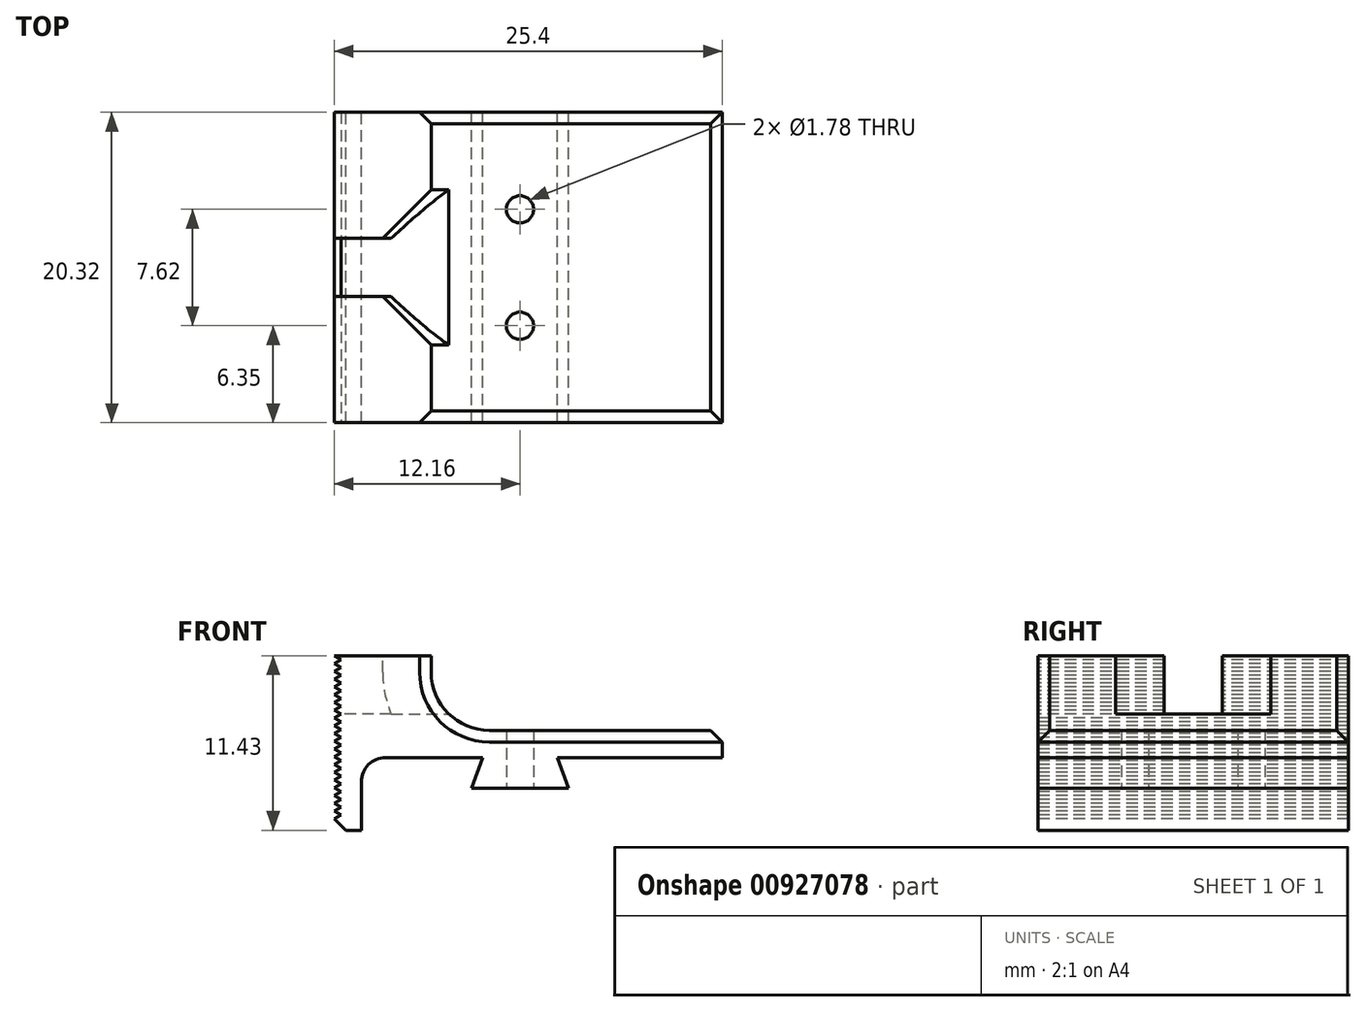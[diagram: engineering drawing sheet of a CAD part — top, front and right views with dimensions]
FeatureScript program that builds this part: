
annotation { "Feature Type Name" : "Feature", "Feature Type Description" : "" }
export const myFeature = defineFeature(function(context is Context, id is Id, definition is map)
    precondition{}
    {
        {
            var Q0;
            Q0=qCreatedBy(makeId("Front.planeOp"),FACE);
            var sketch = newSketch(context, id + "F0", { "sketchPlane" : qUnion([Q0])});
            skLineSegment(sketch, "E0", {"start": v(-0.44, 0) * mm, "end": v(-1.17, -2) * mm});
            skLineSegment(sketch, "E1", {"start": v(-1.17, -2) * mm, "end": v(5.18, -2) * mm});
            skLineSegment(sketch, "E2", {"start": v(5.18, -2) * mm, "end": v(4.44, 0) * mm});
            skLineSegment(sketch, "E3", {"start": v(4.44, 0) * mm, "end": v(15.24, 0) * mm});
            skLineSegment(sketch, "E4", {"start": v(15.24, 0) * mm, "end": v(15.24, 1.78) * mm});
            skLineSegment(sketch, "E5", {"start": v(15.24, 1.78) * mm, "end": v(-3.81, 1.78) * mm});
            skLineSegment(sketch, "E6", {"start": v(-3.81, 1.78) * mm, "end": v(-3.81, 6.67) * mm});
            skLineSegment(sketch, "E7", {"start": v(-3.81, 6.67) * mm, "end": v(-10.16, 6.67) * mm});
            skLineSegment(sketch, "E8", {"start": v(-10.16, 6.67) * mm, "end": v(-10.16, -4.76) * mm});
            skLineSegment(sketch, "E9", {"start": v(-10.16, -4.76) * mm, "end": v(-8.38, -4.76) * mm});
            skLineSegment(sketch, "E10", {"start": v(-8.38, -4.76) * mm, "end": v(-8.38, 0) * mm});
            skLineSegment(sketch, "E11", {"start": v(-8.38, 0) * mm, "end": v(-0.44, 0) * mm});
            skSolve(sketch);
        }
        {
            var Q0;
            Q0=makeQuery(id+"F0.imprint","IMPRINT",FACE,{"disambiguationData":[TD([[makeQuery(id+"F0.imprint","IMPRINT",EDGE,{"derivedFrom":sQuery(id+"F0.wireOp",EDGE,"E0")}),1.0]])]});
            extrude(context, id + "F1", {"entities" : qUnion([Q0]), "endBound" : BoundingType.SYMMETRIC, "depth" : 20.32 * mm, "offsetDistance" : 25.4 * mm});
        }
        {
            var Q0;
            Q0=makeQuery(id+"F1.opExtrude","SWEPT_FACE",FACE,{"disambiguationData":[OSD([sQuery(id+"F0.wireOp",EDGE,"E8")])]});
            var sketch = newSketch(context, id + "F2", { "sketchPlane" : qUnion([Q0])});
            skLineSegment(sketch, "E12.bottom", {"start": v(-1.9, 6.67) * mm, "end": v(1.9, 6.67) * mm});
            skLineSegment(sketch, "E12.top", {"start": v(-1.9, 2.86) * mm, "end": v(1.9, 2.86) * mm});
            skLineSegment(sketch, "E12.left", {"start": v(-1.9, 6.67) * mm, "end": v(-1.9, 2.86) * mm});
            skLineSegment(sketch, "E12.right", {"start": v(1.9, 6.67) * mm, "end": v(1.9, 2.86) * mm});
            skSolve(sketch);
        }
        {
            var Q0;
            Q0=makeQuery(id+"F2.imprint","IMPRINT",FACE,{"disambiguationData":[TD([[makeQuery(id+"F2.imprint","IMPRINT",EDGE,{"derivedFrom":sQuery(id+"F2.wireOp",EDGE,"E12.bottom")}),1.0]])]});
            extrude(context, id + "F3", {"entities" : qUnion([Q0]), "operationType" : NewBodyOperationType.REMOVE, "oppositeDirection" : true, "depth" : 25.4 * mm, "offsetDistance" : 25.4 * mm});
        }
        {
            var Q0;
            Q0=makeQuery(id+"F1.opExtrude","SWEPT_EDGE",EDGE,{"disambiguationData":[OSD([sQuery(id+"F0.wireOp",EDGE,"E10"),sQuery(id+"F0.wireOp",EDGE,"E11")])]});
            fillet(context, id + "F4", {"entities" : qUnion([Q0]), "radius" : 1.59 * mm, "tangentPropagation" : true, "allowEdgeOverflow" : false});
        }
        {
            var Q0;
            Q0=makeQuery(id+"F1.opExtrude","SWEPT_EDGE",EDGE,{"disambiguationData":[OSD([sQuery(id+"F0.wireOp",EDGE,"E5"),sQuery(id+"F0.wireOp",EDGE,"E6")])]});
            fillet(context, id + "F5", {"entities" : qUnion([Q0]), "radius" : 3.8 * mm, "tangentPropagation" : true, "allowEdgeOverflow" : false});
        }
        {
            var Q0;
            Q0=makeQuery(id+"F5.opFillet","BLEND_EDGE",EDGE,{"blendedFrom":[makeQuery(id+"F1.opExtrude","SWEPT_EDGE",EDGE,{"disambiguationData":[OSD([sQuery(id+"F0.wireOp",EDGE,"E5"),sQuery(id+"F0.wireOp",EDGE,"E6")])]}),makeQuery(id+"F3.boolean.opBoolean","COPY",FACE,{"derivedFrom":makeQuery(id+"F3.opExtrude","SWEPT_FACE",FACE,{"disambiguationData":[OSD([sQuery(id+"F2.wireOp",EDGE,"E12.right")])]})})],"blendedInto":[makeQuery(id+"F3.boolean.opBoolean","COPY",FACE,{"derivedFrom":makeQuery(id+"F3.opExtrude","SWEPT_FACE",FACE,{"disambiguationData":[OSD([sQuery(id+"F2.wireOp",EDGE,"E12.right")])]})})]});
            var Q1;
            Q1=makeQuery(id+"F5.opFillet","BLEND_EDGE",EDGE,{"blendedFrom":[makeQuery(id+"F1.opExtrude","SWEPT_EDGE",EDGE,{"disambiguationData":[OSD([sQuery(id+"F0.wireOp",EDGE,"E5"),sQuery(id+"F0.wireOp",EDGE,"E6")])]}),makeQuery(id+"F3.boolean.opBoolean","COPY",FACE,{"derivedFrom":makeQuery(id+"F3.opExtrude","SWEPT_FACE",FACE,{"disambiguationData":[OSD([sQuery(id+"F2.wireOp",EDGE,"E12.left")])]})})],"blendedInto":[makeQuery(id+"F3.boolean.opBoolean","COPY",FACE,{"derivedFrom":makeQuery(id+"F3.opExtrude","SWEPT_FACE",FACE,{"disambiguationData":[OSD([sQuery(id+"F2.wireOp",EDGE,"E12.left")])]})})]});
            chamfer(context, id + "F6", {"entities" : qUnion([Q0, Q1]), "width" : 3.17 * mm, "tangentPropagation" : true});
        }
        {
            var Q0;
            Q0=makeQuery(id+"F1.opExtrude","SWEPT_EDGE",EDGE,{"disambiguationData":[OSD([sQuery(id+"F0.wireOp",EDGE,"E8"),sQuery(id+"F0.wireOp",EDGE,"E9")])]});
            chamfer(context, id + "F7", {"entities" : qUnion([Q0]), "width" : 0.76 * mm, "tangentPropagation" : true});
        }
        {
            var Q0;
            {var subQ0=sQuery(id+"F0.wireOp",EDGE,"E6");var subQ1=sQuery(id+"F0.wireOp",EDGE,"E5");Q0=makeQuery(id+"F5.opFillet","BLEND_EDGE",EDGE,{"blendedFrom":[makeQuery(id+"F1.opExtrude","SWEPT_EDGE",EDGE,{"disambiguationData":[OSD([subQ1,subQ0])]}),makeQuery(id+"F1.opExtrude","CAP_FACE",FACE,{"disambiguationData":[OSD([sQuery(id+"F0.wireOp",EDGE,"E0"),sQuery(id+"F0.wireOp",EDGE,"E1"),sQuery(id+"F0.wireOp",EDGE,"E2"),sQuery(id+"F0.wireOp",EDGE,"E3"),sQuery(id+"F0.wireOp",EDGE,"E4"),subQ1,subQ0,sQuery(id+"F0.wireOp",EDGE,"E7"),sQuery(id+"F0.wireOp",EDGE,"E8"),sQuery(id+"F0.wireOp",EDGE,"E9"),sQuery(id+"F0.wireOp",EDGE,"E10"),sQuery(id+"F0.wireOp",EDGE,"E11")])],"isStart":false})],"blendedInto":[makeQuery(id+"F1.opExtrude","CAP_FACE",FACE,{"disambiguationData":[OSD([sQuery(id+"F0.wireOp",EDGE,"E0"),sQuery(id+"F0.wireOp",EDGE,"E1"),sQuery(id+"F0.wireOp",EDGE,"E2"),sQuery(id+"F0.wireOp",EDGE,"E3"),sQuery(id+"F0.wireOp",EDGE,"E4"),subQ1,subQ0,sQuery(id+"F0.wireOp",EDGE,"E7"),sQuery(id+"F0.wireOp",EDGE,"E8"),sQuery(id+"F0.wireOp",EDGE,"E9"),sQuery(id+"F0.wireOp",EDGE,"E10"),sQuery(id+"F0.wireOp",EDGE,"E11")])],"isStart":false})]});}
            var Q1;
            Q1=makeQuery(id+"F1.opExtrude","CAP_EDGE",EDGE,{"disambiguationData":[OSD([sQuery(id+"F0.wireOp",EDGE,"E5")])],"isStart":false});
            var Q2;
            Q2=makeQuery(id+"F1.opExtrude","CAP_EDGE",EDGE,{"disambiguationData":[OSD([sQuery(id+"F0.wireOp",EDGE,"E5")])],"isStart":true});
            var Q3;
            Q3=makeQuery(id+"F1.opExtrude","SWEPT_EDGE",EDGE,{"disambiguationData":[OSD([sQuery(id+"F0.wireOp",EDGE,"E4"),sQuery(id+"F0.wireOp",EDGE,"E5")])]});
            chamfer(context, id + "F8", {"entities" : qUnion([Q0, Q1, Q2, Q3]), "width" : 0.76 * mm, "tangentPropagation" : true});
        }
        {
            var Q0;
            Q0=makeQuery(id+"F1.opExtrude","SWEPT_FACE",FACE,{"disambiguationData":[OSD([sQuery(id+"F0.wireOp",EDGE,"E1")])]});
            var sketch = newSketch(context, id + "F9", { "sketchPlane" : qUnion([Q0])});
            skPoint(sketch, "E13", {"position": v(2, 3.81) * mm});
            skPoint(sketch, "E14", {"position": v(2, -3.81) * mm});
            skSolve(sketch);
        }
        {
            var Q0;
            Q0=sQuery(id+"F9.wireOp",VERTEX,"E13");
            var Q1;
            Q1=sQuery(id+"F9.wireOp",VERTEX,"E14");
            var Q2;
            Q2=makeQuery(id+"F1.opExtrude","SWEPT_BODY",BODY,{"disambiguationData":[OSD([sQuery(id+"F0.wireOp",EDGE,"E0"),sQuery(id+"F0.wireOp",EDGE,"E1"),sQuery(id+"F0.wireOp",EDGE,"E2"),sQuery(id+"F0.wireOp",EDGE,"E3"),sQuery(id+"F0.wireOp",EDGE,"E4"),sQuery(id+"F0.wireOp",EDGE,"E5"),sQuery(id+"F0.wireOp",EDGE,"E6"),sQuery(id+"F0.wireOp",EDGE,"E7"),sQuery(id+"F0.wireOp",EDGE,"E8"),sQuery(id+"F0.wireOp",EDGE,"E9"),sQuery(id+"F0.wireOp",EDGE,"E10"),sQuery(id+"F0.wireOp",EDGE,"E11")])]});
            hole(context, id + "F10", {"style" : HoleStyle.SIMPLE, "endStyle" : HoleEndStyle.THROUGH, "standardTappedOrClearance" : lookupTablePath({ "standard" : "ANSI", "engagement" : "75%", "pitch" : "56 tpi", "size" : "#2", "type" : "Tapped" }), "standardBlindInLast" : lookupTablePath({ "standard" : "ANSI", "engagement" : "75%", "pitch" : "56 tpi", "size" : "#2", "type" : "Tapped" }), "holeDiameter" : 1.78 * mm, "majorDiameter" : 2.18 * mm, "showTappedDepth" : true, "isTappedThrough" : true, "tappedDepth" : 12.7 * mm, "tapClearance" : 3, "locations" : qUnion([Q0, Q1]), "scope" : qUnion([Q2])});
        }
        {
            var Q0;
            Q0=makeQuery(id+"F1.opExtrude","CAP_FACE",FACE,{"disambiguationData":[OSD([sQuery(id+"F0.wireOp",EDGE,"E0"),sQuery(id+"F0.wireOp",EDGE,"E1"),sQuery(id+"F0.wireOp",EDGE,"E2"),sQuery(id+"F0.wireOp",EDGE,"E3"),sQuery(id+"F0.wireOp",EDGE,"E4"),sQuery(id+"F0.wireOp",EDGE,"E5"),sQuery(id+"F0.wireOp",EDGE,"E6"),sQuery(id+"F0.wireOp",EDGE,"E7"),sQuery(id+"F0.wireOp",EDGE,"E8"),sQuery(id+"F0.wireOp",EDGE,"E9"),sQuery(id+"F0.wireOp",EDGE,"E10"),sQuery(id+"F0.wireOp",EDGE,"E11")])],"isStart":false});
            var sketch = newSketch(context, id + "F11", { "sketchPlane" : qUnion([Q0])});
            skLineSegment(sketch, "E15", {"start": v(-10.16, 7.68) * mm, "end": v(-9.72, 7.43) * mm});
            skLineSegment(sketch, "E16", {"start": v(-9.72, 7.43) * mm, "end": v(-10.16, 7.18) * mm});
            skLineSegment(sketch, "E17.1.0.0", {"start": v(-9.72, 6.92) * mm, "end": v(-10.16, 6.67) * mm});
            skLineSegment(sketch, "E17.1.0.1", {"start": v(-10.16, 7.18) * mm, "end": v(-9.72, 6.92) * mm});
            skLineSegment(sketch, "E17.2.0.0", {"start": v(-9.72, 6.41) * mm, "end": v(-10.16, 6.16) * mm});
            skLineSegment(sketch, "E17.2.0.1", {"start": v(-10.16, 6.67) * mm, "end": v(-9.72, 6.41) * mm});
            skLineSegment(sketch, "E17.3.0.0", {"start": v(-9.72, 5.9) * mm, "end": v(-10.16, 5.65) * mm});
            skLineSegment(sketch, "E17.3.0.1", {"start": v(-10.16, 6.16) * mm, "end": v(-9.72, 5.9) * mm});
            skLineSegment(sketch, "E17.4.0.0", {"start": v(-9.72, 5.4) * mm, "end": v(-10.16, 5.14) * mm});
            skLineSegment(sketch, "E17.4.0.1", {"start": v(-10.16, 5.65) * mm, "end": v(-9.72, 5.4) * mm});
            skLineSegment(sketch, "E17.5.0.0", {"start": v(-9.72, 4.89) * mm, "end": v(-10.16, 4.64) * mm});
            skLineSegment(sketch, "E17.5.0.1", {"start": v(-10.16, 5.14) * mm, "end": v(-9.72, 4.89) * mm});
            skLineSegment(sketch, "E17.6.0.0", {"start": v(-9.72, 4.38) * mm, "end": v(-10.16, 4.13) * mm});
            skLineSegment(sketch, "E17.6.0.1", {"start": v(-10.16, 4.64) * mm, "end": v(-9.72, 4.38) * mm});
            skLineSegment(sketch, "E17.7.0.0", {"start": v(-9.72, 3.87) * mm, "end": v(-10.16, 3.62) * mm});
            skLineSegment(sketch, "E17.7.0.1", {"start": v(-10.16, 4.13) * mm, "end": v(-9.72, 3.87) * mm});
            skLineSegment(sketch, "E17.8.0.0", {"start": v(-9.72, 3.37) * mm, "end": v(-10.16, 3.11) * mm});
            skLineSegment(sketch, "E17.8.0.1", {"start": v(-10.16, 3.62) * mm, "end": v(-9.72, 3.37) * mm});
            skLineSegment(sketch, "E17.9.0.0", {"start": v(-9.72, 2.86) * mm, "end": v(-10.16, 2.6) * mm});
            skLineSegment(sketch, "E17.9.0.1", {"start": v(-10.16, 3.11) * mm, "end": v(-9.72, 2.86) * mm});
            skLineSegment(sketch, "E17.10.0.0", {"start": v(-9.72, 2.35) * mm, "end": v(-10.16, 2.1) * mm});
            skLineSegment(sketch, "E17.10.0.1", {"start": v(-10.16, 2.6) * mm, "end": v(-9.72, 2.35) * mm});
            skLineSegment(sketch, "E17.11.0.0", {"start": v(-9.72, 1.84) * mm, "end": v(-10.16, 1.59) * mm});
            skLineSegment(sketch, "E17.11.0.1", {"start": v(-10.16, 2.1) * mm, "end": v(-9.72, 1.84) * mm});
            skLineSegment(sketch, "E17.12.0.0", {"start": v(-9.72, 1.33) * mm, "end": v(-10.16, 1.08) * mm});
            skLineSegment(sketch, "E17.12.0.1", {"start": v(-10.16, 1.59) * mm, "end": v(-9.72, 1.33) * mm});
            skLineSegment(sketch, "E17.13.0.0", {"start": v(-9.72, 0.83) * mm, "end": v(-10.16, 0.57) * mm});
            skLineSegment(sketch, "E17.13.0.1", {"start": v(-10.16, 1.08) * mm, "end": v(-9.72, 0.83) * mm});
            skLineSegment(sketch, "E17.14.0.0", {"start": v(-9.72, 0.32) * mm, "end": v(-10.16, 0.06) * mm});
            skLineSegment(sketch, "E17.14.0.1", {"start": v(-10.16, 0.57) * mm, "end": v(-9.72, 0.32) * mm});
            skLineSegment(sketch, "E17.15.0.0", {"start": v(-9.72, -0.2) * mm, "end": v(-10.16, -0.44) * mm});
            skLineSegment(sketch, "E17.15.0.1", {"start": v(-10.16, 0.06) * mm, "end": v(-9.72, -0.2) * mm});
            skLineSegment(sketch, "E17.16.0.0", {"start": v(-9.72, -0.7) * mm, "end": v(-10.16, -0.95) * mm});
            skLineSegment(sketch, "E17.16.0.1", {"start": v(-10.16, -0.44) * mm, "end": v(-9.72, -0.7) * mm});
            skLineSegment(sketch, "E17.17.0.0", {"start": v(-9.72, -1.2) * mm, "end": v(-10.16, -1.46) * mm});
            skLineSegment(sketch, "E17.17.0.1", {"start": v(-10.16, -0.95) * mm, "end": v(-9.72, -1.2) * mm});
            skLineSegment(sketch, "E17.18.0.0", {"start": v(-9.72, -1.71) * mm, "end": v(-10.16, -1.97) * mm});
            skLineSegment(sketch, "E17.18.0.1", {"start": v(-10.16, -1.46) * mm, "end": v(-9.72, -1.71) * mm});
            skLineSegment(sketch, "E17.19.0.0", {"start": v(-9.72, -2.22) * mm, "end": v(-10.16, -2.48) * mm});
            skLineSegment(sketch, "E17.19.0.1", {"start": v(-10.16, -1.97) * mm, "end": v(-9.72, -2.22) * mm});
            skLineSegment(sketch, "E17.20.0.0", {"start": v(-9.72, -2.73) * mm, "end": v(-10.16, -2.98) * mm});
            skLineSegment(sketch, "E17.20.0.1", {"start": v(-10.16, -2.48) * mm, "end": v(-9.72, -2.73) * mm});
            skLineSegment(sketch, "E17.21.0.0", {"start": v(-9.72, -3.24) * mm, "end": v(-10.16, -3.5) * mm});
            skLineSegment(sketch, "E17.21.0.1", {"start": v(-10.16, -2.98) * mm, "end": v(-9.72, -3.24) * mm});
            skLineSegment(sketch, "E17.22.0.0", {"start": v(-9.72, -3.75) * mm, "end": v(-10.16, -4) * mm});
            skLineSegment(sketch, "E17.22.0.1", {"start": v(-10.16, -3.5) * mm, "end": v(-9.72, -3.75) * mm});
            skLineSegment(sketch, "E17.direction1", {"start": v(-10.16, 7.18) * mm, "end": v(-10.16, 6.67) * mm, "construction": true});
            skSolve(sketch);
        }
        {
            var Q0;
            {var subQ0=sQuery(id+"F11.wireOp",EDGE,"E17.22.0.0");Q0=makeQuery(id+"F11.imprint","IMPRINT",FACE,{"disambiguationData":[TD([[makeQuery(id+"F11.imprint","IMPRINT",EDGE,{"derivedFrom":subQ0}),-1.0]])]});}
            var Q1;
            {var subQ0=sQuery(id+"F11.wireOp",EDGE,"E17.21.0.0");Q1=makeQuery(id+"F11.imprint","IMPRINT",FACE,{"disambiguationData":[TD([[makeQuery(id+"F11.imprint","IMPRINT",EDGE,{"derivedFrom":subQ0}),-1.0]])]});}
            var Q2;
            {var subQ0=sQuery(id+"F11.wireOp",EDGE,"E17.20.0.0");Q2=makeQuery(id+"F11.imprint","IMPRINT",FACE,{"disambiguationData":[TD([[makeQuery(id+"F11.imprint","IMPRINT",EDGE,{"derivedFrom":subQ0}),-1.0]])]});}
            var Q3;
            {var subQ0=sQuery(id+"F11.wireOp",EDGE,"E17.19.0.0");Q3=makeQuery(id+"F11.imprint","IMPRINT",FACE,{"disambiguationData":[TD([[makeQuery(id+"F11.imprint","IMPRINT",EDGE,{"derivedFrom":subQ0}),-1.0]])]});}
            var Q4;
            {var subQ0=sQuery(id+"F11.wireOp",EDGE,"E17.18.0.0");Q4=makeQuery(id+"F11.imprint","IMPRINT",FACE,{"disambiguationData":[TD([[makeQuery(id+"F11.imprint","IMPRINT",EDGE,{"derivedFrom":subQ0}),-1.0]])]});}
            var Q5;
            {var subQ0=sQuery(id+"F11.wireOp",EDGE,"E17.17.0.0");Q5=makeQuery(id+"F11.imprint","IMPRINT",FACE,{"disambiguationData":[TD([[makeQuery(id+"F11.imprint","IMPRINT",EDGE,{"derivedFrom":subQ0}),-1.0]])]});}
            var Q6;
            {var subQ0=sQuery(id+"F11.wireOp",EDGE,"E17.16.0.0");Q6=makeQuery(id+"F11.imprint","IMPRINT",FACE,{"disambiguationData":[TD([[makeQuery(id+"F11.imprint","IMPRINT",EDGE,{"derivedFrom":subQ0}),-1.0]])]});}
            var Q7;
            {var subQ0=sQuery(id+"F11.wireOp",EDGE,"E17.15.0.0");Q7=makeQuery(id+"F11.imprint","IMPRINT",FACE,{"disambiguationData":[TD([[makeQuery(id+"F11.imprint","IMPRINT",EDGE,{"derivedFrom":subQ0}),-1.0]])]});}
            var Q8;
            {var subQ0=sQuery(id+"F11.wireOp",EDGE,"E17.14.0.0");Q8=makeQuery(id+"F11.imprint","IMPRINT",FACE,{"disambiguationData":[TD([[makeQuery(id+"F11.imprint","IMPRINT",EDGE,{"derivedFrom":subQ0}),-1.0]])]});}
            var Q9;
            {var subQ0=sQuery(id+"F11.wireOp",EDGE,"E17.13.0.0");Q9=makeQuery(id+"F11.imprint","IMPRINT",FACE,{"disambiguationData":[TD([[makeQuery(id+"F11.imprint","IMPRINT",EDGE,{"derivedFrom":subQ0}),-1.0]])]});}
            var Q10;
            {var subQ0=sQuery(id+"F11.wireOp",EDGE,"E17.12.0.0");Q10=makeQuery(id+"F11.imprint","IMPRINT",FACE,{"disambiguationData":[TD([[makeQuery(id+"F11.imprint","IMPRINT",EDGE,{"derivedFrom":subQ0}),-1.0]])]});}
            var Q11;
            {var subQ0=sQuery(id+"F11.wireOp",EDGE,"E17.11.0.0");Q11=makeQuery(id+"F11.imprint","IMPRINT",FACE,{"disambiguationData":[TD([[makeQuery(id+"F11.imprint","IMPRINT",EDGE,{"derivedFrom":subQ0}),-1.0]])]});}
            var Q12;
            {var subQ0=sQuery(id+"F11.wireOp",EDGE,"E17.10.0.0");Q12=makeQuery(id+"F11.imprint","IMPRINT",FACE,{"disambiguationData":[TD([[makeQuery(id+"F11.imprint","IMPRINT",EDGE,{"derivedFrom":subQ0}),-1.0]])]});}
            var Q13;
            {var subQ0=sQuery(id+"F11.wireOp",EDGE,"E17.9.0.0");Q13=makeQuery(id+"F11.imprint","IMPRINT",FACE,{"disambiguationData":[TD([[makeQuery(id+"F11.imprint","IMPRINT",EDGE,{"derivedFrom":subQ0}),-1.0]])]});}
            var Q14;
            {var subQ0=sQuery(id+"F11.wireOp",EDGE,"E17.8.0.0");Q14=makeQuery(id+"F11.imprint","IMPRINT",FACE,{"disambiguationData":[TD([[makeQuery(id+"F11.imprint","IMPRINT",EDGE,{"derivedFrom":subQ0}),-1.0]])]});}
            var Q15;
            {var subQ0=sQuery(id+"F11.wireOp",EDGE,"E17.7.0.0");Q15=makeQuery(id+"F11.imprint","IMPRINT",FACE,{"disambiguationData":[TD([[makeQuery(id+"F11.imprint","IMPRINT",EDGE,{"derivedFrom":subQ0}),-1.0]])]});}
            var Q16;
            {var subQ0=sQuery(id+"F11.wireOp",EDGE,"E17.6.0.0");Q16=makeQuery(id+"F11.imprint","IMPRINT",FACE,{"disambiguationData":[TD([[makeQuery(id+"F11.imprint","IMPRINT",EDGE,{"derivedFrom":subQ0}),-1.0]])]});}
            var Q17;
            {var subQ0=sQuery(id+"F11.wireOp",EDGE,"E17.5.0.0");Q17=makeQuery(id+"F11.imprint","IMPRINT",FACE,{"disambiguationData":[TD([[makeQuery(id+"F11.imprint","IMPRINT",EDGE,{"derivedFrom":subQ0}),-1.0]])]});}
            var Q18;
            {var subQ0=sQuery(id+"F11.wireOp",EDGE,"E17.4.0.0");Q18=makeQuery(id+"F11.imprint","IMPRINT",FACE,{"disambiguationData":[TD([[makeQuery(id+"F11.imprint","IMPRINT",EDGE,{"derivedFrom":subQ0}),-1.0]])]});}
            var Q19;
            {var subQ0=sQuery(id+"F11.wireOp",EDGE,"E17.3.0.0");Q19=makeQuery(id+"F11.imprint","IMPRINT",FACE,{"disambiguationData":[TD([[makeQuery(id+"F11.imprint","IMPRINT",EDGE,{"derivedFrom":subQ0}),-1.0]])]});}
            var Q20;
            {var subQ0=sQuery(id+"F11.wireOp",EDGE,"E17.2.0.0");Q20=makeQuery(id+"F11.imprint","IMPRINT",FACE,{"disambiguationData":[TD([[makeQuery(id+"F11.imprint","IMPRINT",EDGE,{"derivedFrom":subQ0}),-1.0]])]});}
            extrude(context, id + "F12", {"entities" : qUnion([Q0, Q1, Q2, Q3, Q4, Q5, Q6, Q7, Q8, Q9, Q10, Q11, Q12, Q13, Q14, Q15, Q16, Q17, Q18, Q19, Q20]), "operationType" : NewBodyOperationType.REMOVE, "oppositeDirection" : true, "depth" : 25.4 * mm, "offsetDistance" : 25.4 * mm});
        }
    });
